# Revit family: Division_Twelve-Twigz-Cafe_Chair-
name_source: partatom
category: Furniture
units: mm (PartAtom-declared; Revit-internal decimal feet)

## family parameters
Always vertical = Yes
Cut with Voids When Loaded = No
OmniClass Number = 23.40.20.00
OmniClass Title = General Furniture and Specialties
Room Calculation Point = No
Shared = No
Work Plane-Based = No

## types (4) — shared parameters
Assembly Code = E2020200
Default Elevation = 0"
Depth = 19 1/2"
Height = 32"
Keynote = 12500
Low Emitting Finish = Yes
Low Emitting Material = Yes
Manufacturer = Division Twelve
Product Documentation Link = https://division12.com
Revit Model Built By = https://servex-us.com
Salvage or Reuse = Yes
Type Comments = Twigz
URL = https://division12.com
Width = 17 21/32"
zero-valued in all types: Percentage of Recycled Content

## per-type parameters (varying)
| type | Description | S-1 | S-2 | S-3 |
| 115101A | Café chair with white oak seat | Yes | No | No |
| 115101B | Café chair with upholstered seat | No | Yes | No |
| 115101C | Café chair with steel seat | No | No | Yes |
| 115101F | Café chair with stained oak seat | Yes | No | No |

note: column(s) folded — value = type name in every type: Model

## geometry (parser evidence)
native form markers: Sweep x5
no freeform markers — native parametric forms only
